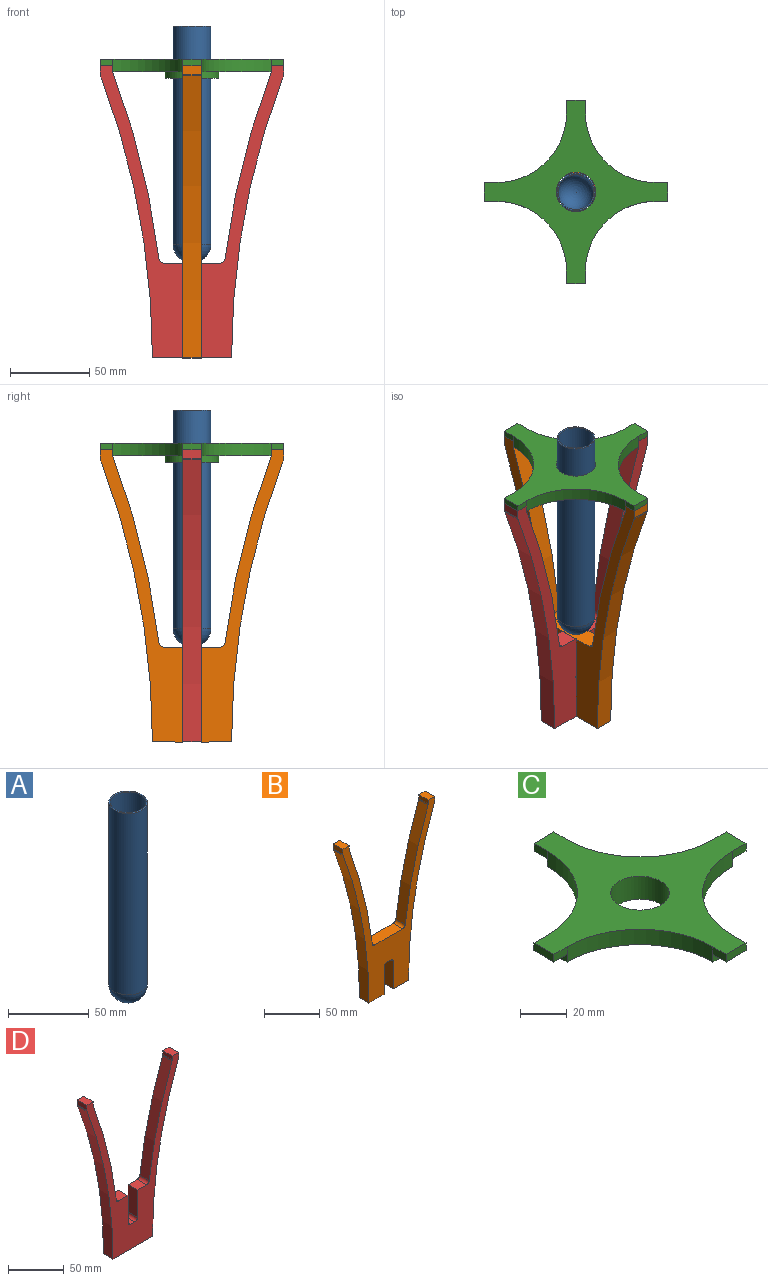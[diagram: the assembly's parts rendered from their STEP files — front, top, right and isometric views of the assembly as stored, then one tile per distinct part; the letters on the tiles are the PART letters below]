
ASSEMBLY  parts=4 mates=6
PART A: 5 faces, bbox 26x26x150 mm
  f0: sphere r=12mm, area 904.8mm2, adj f1
  f1: cylinder r=12mm len=137.6mm, axis (0,0,1), area 10374.8mm2, adj f0,f4
  f2: sphere r=11.2mm, area 788.2mm2, adj f3
  f3: cylinder r=11.2mm len=137.6mm, axis (0,0,1), area 9683.1mm2, adj f2,f4
  f4: torus R=11.6mm, axis (0,0,1), area 91.6mm2, adj f1,f3
PART B: 26 faces, bbox 116x12x185 mm
  f0: plane 19x12mm, normal (0,0,-1), area 228mm2, adj f1,f2,f5,f12
  f1: plane 185x116mm, normal (0,-1,0), area 4814.7mm2, adj f0,f3,f4,f5,f6,f7,f8,f9
  f2: plane 185x116mm, normal (0,1,0), area 4814.7mm2, adj f0,f3,f4,f5,f6,f7,f8,f9
  f3: cylinder r=3.25mm len=12mm, axis (0,1,0), area 56.4mm2, adj f1,f2,f4,f11
  f4: plane 35.33x12mm, normal (0,0,1), area 424mm2, adj f1,f2,f3,f16
  f5: cylinder r=501.63mm len=178.38mm, axis (0,1,0), area 2188.4mm2, adj f0,f1,f2,f6
  f6: cylinder r=3.25mm len=12mm, axis (0,1,0), area 14.2mm2, adj f1,f2,f5,f7
  f7: plane 12x5.46mm, normal (1,0,0), area 65.6mm2, adj f1,f2,f6,f8
  f8: plane 12x8mm, normal (0,0,1), area 96mm2, adj f1,f2,f7,f9
  f9: plane 12x4mm, normal (-1,0,0), area 48mm2, adj f1,f2,f8,f10
  f10: cylinder r=3.25mm len=12mm, axis (0,1,0), area 14.1mm2, adj f1,f2,f9,f11
  f11: cylinder r=509.63mm len=117mm, axis (0,1,0), area 1449.6mm2, adj f1,f2,f3,f10
  f12: plane 30x12mm, normal (-1,0,0), area 360mm2, adj f0,f1,f2,f13
  f13: cylinder r=3.25mm len=12mm, axis (0,1,0), area 61.3mm2, adj f1,f2,f12,f14
  f14: plane 12x5.5mm, normal (0,0,-1), area 66mm2, adj f1,f2,f13,f25
  f15: plane 19x12mm, normal (0,0,-1), area 228mm2, adj f1,f2,f17,f24
  f16: cylinder r=3.25mm len=12mm, axis (0,1,0), area 56.4mm2, adj f1,f2,f4,f23
  f17: cylinder r=501.63mm len=178.38mm, axis (0,1,0), area 2188.4mm2, adj f1,f2,f15,f18
  f18: cylinder r=3.25mm len=12mm, axis (0,1,0), area 14.2mm2, adj f1,f2,f17,f19
  f19: plane 12x5.46mm, normal (-1,0,0), area 65.6mm2, adj f1,f2,f18,f20
  f20: plane 12x8mm, normal (0,0,1), area 96mm2, adj f1,f2,f19,f21
  f21: plane 12x4mm, normal (1,0,0), area 48mm2, adj f1,f2,f20,f22
  f22: cylinder r=3.25mm len=12mm, axis (0,1,0), area 14.1mm2, adj f1,f2,f21,f23
  f23: cylinder r=509.63mm len=117mm, axis (0,1,0), area 1449.6mm2, adj f1,f2,f16,f22
  f24: plane 30x12mm, normal (1,0,0), area 360mm2, adj f1,f2,f15,f25
  f25: cylinder r=3.25mm len=12mm, axis (0,1,0), area 61.3mm2, adj f1,f2,f14,f24
PART C: 29 faces, bbox 116x116x12 mm
  f0: plane 8x4mm, normal (1,0,0), area 32mm2, adj f1,f3,f4,f7
  f1: plane 12x4mm, normal (0,1,0), area 48mm2, adj f0,f4,f7,f18
  f2: cylinder r=12.5mm len=25mm, axis (0,0,-1), area 942.5mm2, adj f4,f28
  f3: cylinder r=44mm len=44mm, axis (0,0,-1), area 552.9mm2, adj f0,f4,f5,f6,f8,f10
  f4: plane 116x116mm, normal (0,0,1), area 3811mm2, adj f0,f1,f2,f3,f8,f9,f12,f13
  f5: plane 100x100mm, normal (0,0,-1), area 3010mm2, adj f3,f6,f10,f14,f15,f19,f22,f25
  f6: plane 12x4mm, normal (0,1,0), area 48mm2, adj f3,f5,f7,f19
  f7: plane 12x8mm, normal (0,0,-1), area 96mm2, adj f0,f1,f6,f18
  f8: plane 8x4mm, normal (0,1,0), area 32mm2, adj f3,f4,f9,f11
  f9: plane 12x4mm, normal (1,0,0), area 48mm2, adj f4,f8,f11,f17
  f10: plane 12x4mm, normal (1,0,0), area 48mm2, adj f3,f5,f11,f14
  f11: plane 12x8mm, normal (0,0,-1), area 96mm2, adj f8,f9,f10,f17
  f12: plane 8x4mm, normal (1,0,0), area 32mm2, adj f4,f13,f14,f16
  f13: plane 12x4mm, normal (0,-1,0), area 48mm2, adj f4,f12,f16,f24
  f14: cylinder r=44mm len=44mm, axis (0,0,-1), area 552.9mm2, adj f4,f5,f10,f12,f15,f17
  f15: plane 12x4mm, normal (0,-1,0), area 48mm2, adj f5,f14,f16,f25
  f16: plane 12x8mm, normal (0,0,-1), area 96mm2, adj f12,f13,f15,f24
  f17: plane 8x4mm, normal (0,-1,0), area 32mm2, adj f4,f9,f11,f14
  f18: plane 8x4mm, normal (-1,0,0), area 32mm2, adj f1,f4,f7,f19
  f19: cylinder r=44mm len=44mm, axis (0,0,-1), area 552.9mm2, adj f4,f5,f6,f18,f20,f22
  f20: plane 8x4mm, normal (0,1,0), area 32mm2, adj f4,f19,f21,f23
  f21: plane 12x4mm, normal (-1,0,0), area 48mm2, adj f4,f20,f23,f26
  f22: plane 12x4mm, normal (-1,0,0), area 48mm2, adj f5,f19,f23,f25
  f23: plane 12x8mm, normal (0,0,-1), area 96mm2, adj f20,f21,f22,f26
  f24: plane 8x4mm, normal (-1,0,0), area 32mm2, adj f4,f13,f16,f25
  f25: cylinder r=44mm len=44mm, axis (0,0,-1), area 552.9mm2, adj f4,f5,f15,f22,f24,f26
  f26: plane 8x4mm, normal (0,-1,0), area 32mm2, adj f4,f21,f23,f25
  f27: cylinder r=17mm len=34mm, axis (0,0,1), area 427.3mm2, adj f5,f28
  f28: plane 34x34mm, normal (0,0,-1), area 417mm2, adj f2,f27
PART D: 26 faces, bbox 116x12x185 mm
  f0: plane 12x11.67mm, normal (0,0,1), area 140mm2, adj f1,f2,f3,f14
  f1: plane 185x116mm, normal (0,-1,0), area 4814.7mm2, adj f0,f3,f4,f5,f6,f7,f8,f9
  f2: plane 185x116mm, normal (0,1,0), area 4814.7mm2, adj f0,f3,f4,f5,f6,f7,f8,f9
  f3: cylinder r=3.25mm len=12mm, axis (0,1,0), area 56.4mm2, adj f0,f1,f2,f11
  f4: plane 50x12mm, normal (0,0,-1), area 600mm2, adj f1,f2,f5,f17
  f5: cylinder r=501.63mm len=178.38mm, axis (0,1,0), area 2188.4mm2, adj f1,f2,f4,f6
  f6: cylinder r=3.25mm len=12mm, axis (0,1,0), area 14.2mm2, adj f1,f2,f5,f7
  f7: plane 12x5.46mm, normal (1,0,0), area 65.6mm2, adj f1,f2,f6,f8
  f8: plane 12x8mm, normal (0,0,1), area 96mm2, adj f1,f2,f7,f9
  f9: plane 12x4mm, normal (-1,0,0), area 48mm2, adj f1,f2,f8,f10
  f10: cylinder r=3.25mm len=12mm, axis (0,1,0), area 14.1mm2, adj f1,f2,f9,f11
  f11: cylinder r=509.63mm len=117mm, axis (0,1,0), area 1449.6mm2, adj f1,f2,f3,f10
  f12: plane 12x5.5mm, normal (0,0,1), area 66mm2, adj f1,f2,f13,f24
  f13: cylinder r=3.25mm len=12mm, axis (0,1,0), area 61.3mm2, adj f1,f2,f12,f14
  f14: plane 30x12mm, normal (-1,0,0), area 360mm2, adj f0,f1,f2,f13
  f15: plane 12x11.67mm, normal (0,0,1), area 140mm2, adj f1,f2,f16,f25
  f16: cylinder r=3.25mm len=12mm, axis (0,1,0), area 56.4mm2, adj f1,f2,f15,f23
  f17: cylinder r=501.63mm len=178.38mm, axis (0,1,0), area 2188.4mm2, adj f1,f2,f4,f18
  f18: cylinder r=3.25mm len=12mm, axis (0,1,0), area 14.2mm2, adj f1,f2,f17,f19
  f19: plane 12x5.46mm, normal (-1,0,0), area 65.6mm2, adj f1,f2,f18,f20
  f20: plane 12x8mm, normal (0,0,1), area 96mm2, adj f1,f2,f19,f21
  f21: plane 12x4mm, normal (1,0,0), area 48mm2, adj f1,f2,f20,f22
  f22: cylinder r=3.25mm len=12mm, axis (0,1,0), area 14.1mm2, adj f1,f2,f21,f23
  f23: cylinder r=509.63mm len=117mm, axis (0,1,0), area 1449.6mm2, adj f1,f2,f16,f22
  f24: cylinder r=3.25mm len=12mm, axis (0,1,0), area 61.3mm2, adj f1,f2,f12,f25
  f25: plane 30x12mm, normal (1,0,0), area 360mm2, adj f1,f2,f15,f24
PLACE A t=(0,0,60)mm
PLACE B rot(axis=(0,0,-1),90deg) t=(0,0,0)mm
PLACE C t=(0,0,185)mm
PLACE D at identity fixed
MATE planar B.f4 <-> D.f15  axis (0,0,1) through (0,0,60)mm
MATE slider B.f4 <-> D.f12  axis (0,0,1) through (0,0,60)mm
MATE planar C.f23 <-> D.f20  axis (0,0,-1) through (-54,0,185)mm
MATE slider C.f2 <-> B.f4  axis (0,0,-1) through (0,0,189)mm
MATE parallel B.f1 <-> D.f25  axis (-1,0,0) through (-6,0,71.41)mm
MATE slider C.f2 <-> A.f1  axis (0,0,-1) through (0,0,183)mm
